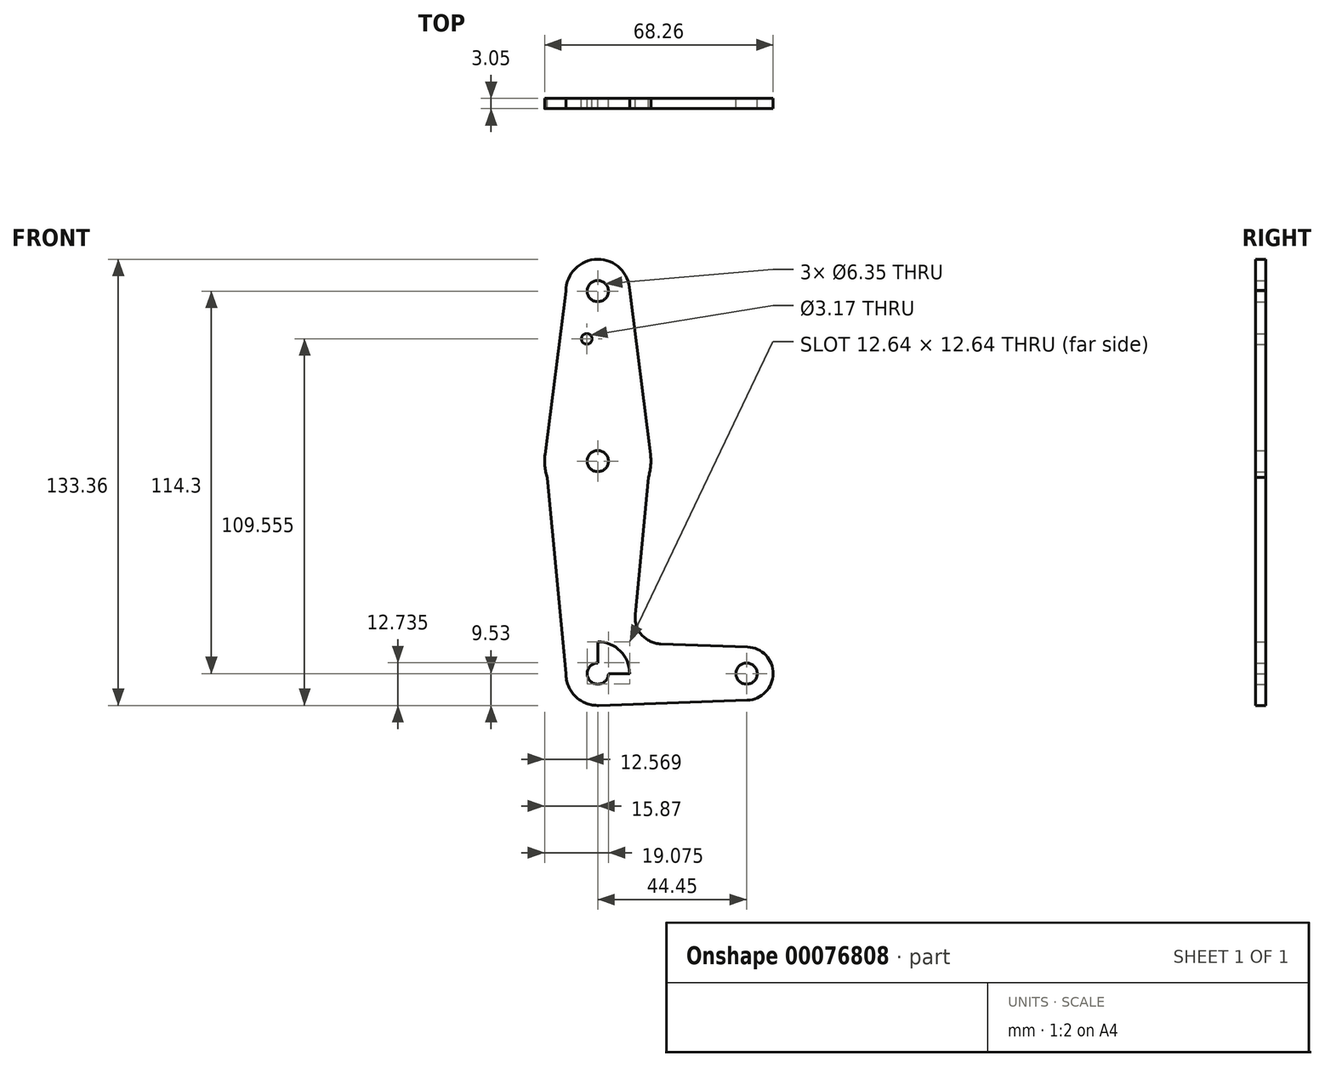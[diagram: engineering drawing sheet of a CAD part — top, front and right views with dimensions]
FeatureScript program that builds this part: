
annotation { "Feature Type Name" : "Feature", "Feature Type Description" : "" }
export const myFeature = defineFeature(function(context is Context, id is Id, definition is map)
    precondition{}
    {
        {
            var Q0;
            Q0=qCreatedBy(makeId("Front.planeOp"),FACE);
            var sketch = newSketch(context, id + "F0", { "sketchPlane" : qUnion([Q0])});
            skCircle(sketch, "E0", {"center": v(0, 114.3) * mm, "radius": 9.52 * mm});
            skCircle(sketch, "E1", {"center": v(0, 63.5) * mm, "radius": 15.88 * mm});
            skCircle(sketch, "E2", {"center": v(0, 0) * mm, "radius": 9.53 * mm});
            skCircle(sketch, "E3", {"center": v(44.45, 0) * mm, "radius": 7.94 * mm});
            skLineSegment(sketch, "E4", {"start": v(0, 114.3) * mm, "end": v(0, 0) * mm});
            skLineSegment(sketch, "E5", {"start": v(44.45, 0) * mm, "end": v(0, 0) * mm});
            skLineSegment(sketch, "E6", {"start": v(-9.52, 114.3) * mm, "end": v(-15.75, 65.5) * mm});
            skLineSegment(sketch, "E7", {"start": v(9.52, 114.44) * mm, "end": v(15.75, 65.5) * mm});
            skPoint(sketch, "E8.centerSnap0", {"position": v(-12.64, 89.9) * mm});
            skCircle(sketch, "E9", {"center": v(0, 63.5) * mm, "radius": 3.18 * mm});
            skLineSegment(sketch, "E10", {"start": v(0, 63.5) * mm, "end": v(0, 100.03) * mm});
            skCircle(sketch, "E11", {"center": v(0, 114.3) * mm, "radius": 3.18 * mm});
            skCircle(sketch, "E12", {"center": v(0, 0) * mm, "radius": 9.52 * mm});
            skCircle(sketch, "E13", {"center": v(0, 0) * mm, "radius": 3.18 * mm});
            skCircle(sketch, "E14", {"center": v(44.45, 0) * mm, "radius": 3.18 * mm});
            skCircle(sketch, "E15", {"center": v(-3.3, 100.03) * mm, "radius": 1.59 * mm});
            skLineSegment(sketch, "E16", {"start": v(-9.52, 0) * mm, "end": v(-15.75, 65.5) * mm});
            skPoint(sketch, "E17.newPointA", {"position": v(9.53, 0) * mm});
            skPoint(sketch, "E17.newPointB", {"position": v(0, 9.53) * mm});
            skLineSegment(sketch, "E18", {"start": v(44.65, -7.93) * mm, "end": v(0.34, -9.52) * mm});
            skLineSegment(sketch, "E19", {"start": v(18.82, 8.85) * mm, "end": v(44.73, 7.93) * mm});
            skLineSegment(sketch, "E20", {"start": v(15.75, 65.5) * mm, "end": v(11.2, 17.55) * mm});
            skArc(sketch, "E21.filletArc", {"start": v(11.2, 17.55) * mm, "mid": v(13.13, 11.56) * mm, "end": v(18.82, 8.85) * mm});
            skSolve(sketch);
        }
        {
            var Q0;
            Q0 = qSketchRegion(id + "F0", true);
            var Q1;
            {var subQ0=sQuery(id+"F0.wireOp",EDGE,"E12");var subQ1=sQuery(id+"F0.wireOp",EDGE,"E4");var subQ2=makeQuery(id+"F0.imprint","INTERSECT",VERTEX,{"derivedFrom":[subQ1,subQ0]});Q1=makeQuery(id+"F0.imprint","IMPRINT",FACE,{"disambiguationData":[TD([[makeQuery(id+"F0.imprint","IMPRINT",EDGE,{"disambiguationData":[TD([[subQ2,-1.0]])],"derivedFrom":subQ1}),1.0]])]});}
            extrude(context, id + "F1", {"entities" : qUnion([Q0, Q1]), "depth" : 3.05 * mm});
        }
    });
